# Revit family: 17L-CW
name_source: partatom
category: Lighting Fixtures
revit_build: Autodesk Revit 2014 (Build: 20130308_1515(x64)
units: mm (PartAtom-declared; Revit-internal decimal feet)

## types (3) — shared parameters
Apparent Load = 3 VA
Assembly Code = D5020200
Backbox = Hubbell- Paint - Matte White
Circuiting = 1 Circuit
Color Filter = 16777215
Default Elevation = 48 "
Description = Indirect Light Coves by Armstrong
Dimming Lamp Color Temperature Shift = <None>
Emit Shape Visible in Rendering = No
Emit from Rectangle Length = 1.5 "
Glass = Hubbell - White Glass
Lamp = LED
Load Classification = Lighting
Manufacturer = Litecontrol Lighting
Model = 17L-CW
Mounting = Armstrong Axiom Cove Wall
Nominal Watts = 3 W
Photometric Link = https://www.hubbell.com
Photometric Notes = More IES files download on Photometric Link
Photometric Web File = 17L-CW-AI-02-C1-35K-I030.IES
Power Factor = 1
Product Documentation Link = https://hubbellcdn.com
Product Page URL = https://www.hubbell.com
Tilt Angle = 90.00°
Type Comments = Lighting Fixture
URL = https://www.hubbell.com
Voltage = 120 V
Warranty = 5 years warranty
Wattage Comments = 133 Lumens/Watt

## per-type parameters (varying)
| type | Emit from Rectangle Width | zz Length 1 |
| 17L-CW-04 | 47.75 " | 48 " |
| 17L-CW-02 | 23.75 " | 24 " |
| 17L-CW-03 | 35.75 " | 36 " |

## geometry (parser evidence)
native form markers: Sweep x3
no freeform markers — native parametric forms only
